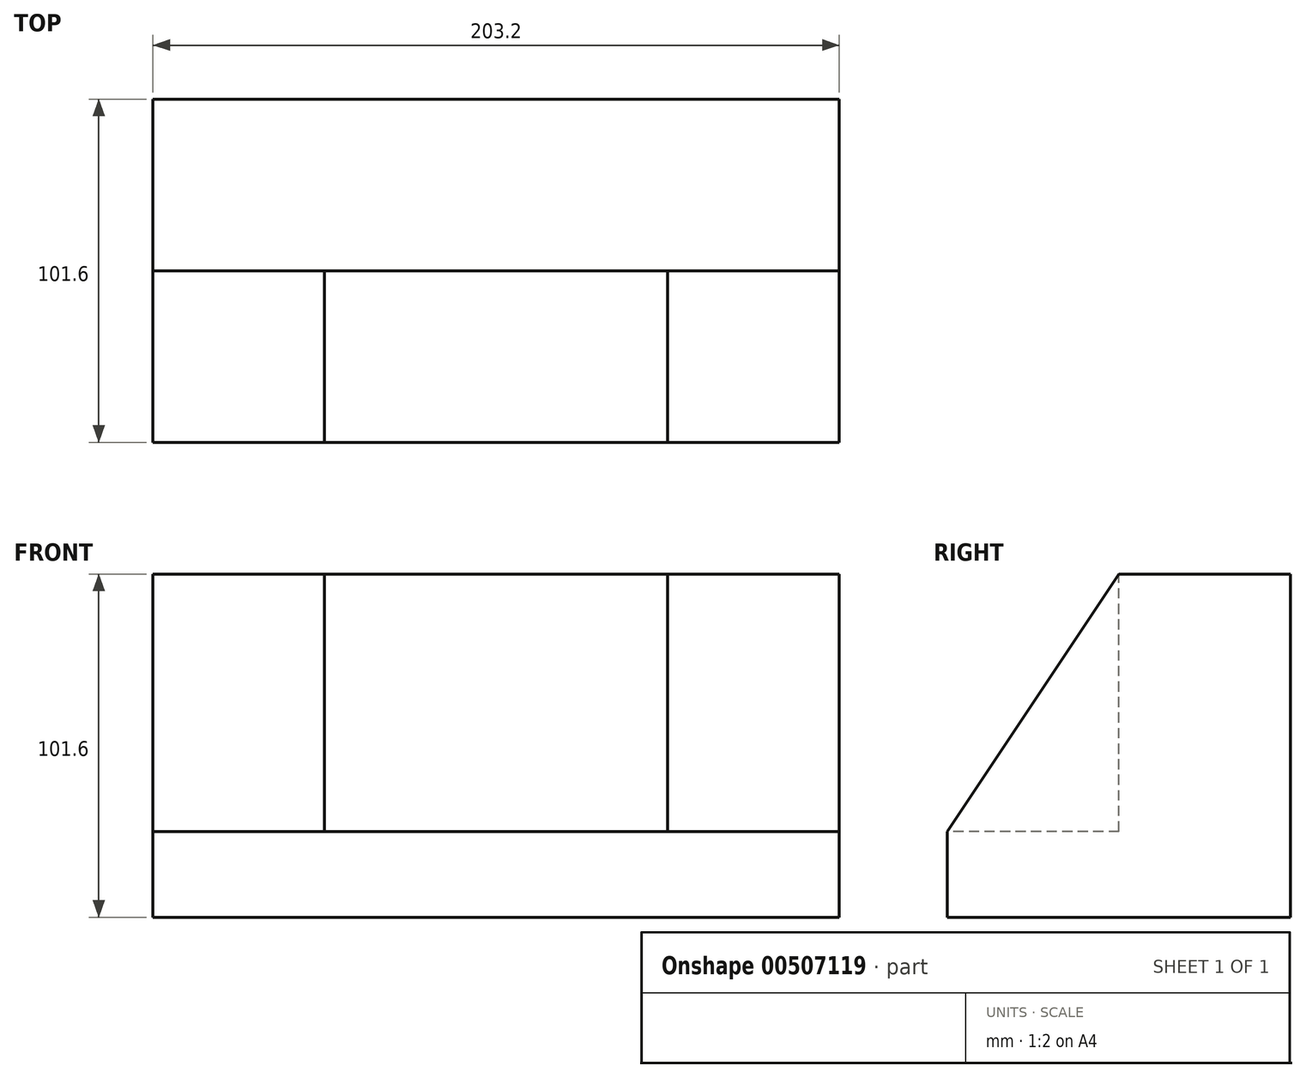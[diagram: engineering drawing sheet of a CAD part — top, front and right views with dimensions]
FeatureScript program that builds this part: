
annotation { "Feature Type Name" : "Feature", "Feature Type Description" : "" }
export const myFeature = defineFeature(function(context is Context, id is Id, definition is map)
    precondition{}
    {
        {
            var Q0;
            Q0=qCreatedBy(makeId("Top.planeOp"),FACE);
            var sketch = newSketch(context, id + "F0", { "sketchPlane" : qUnion([Q0])});
            skLineSegment(sketch, "E0.bottom", {"start": v(101.6, 50.8) * mm, "end": v(-101.6, 50.8) * mm});
            skLineSegment(sketch, "E0.top", {"start": v(101.6, -50.8) * mm, "end": v(-101.6, -50.8) * mm});
            skLineSegment(sketch, "E0.left", {"start": v(101.6, 50.8) * mm, "end": v(101.6, -50.8) * mm});
            skLineSegment(sketch, "E0.right", {"start": v(-101.6, 50.8) * mm, "end": v(-101.6, -50.8) * mm});
            skPoint(sketch, "E0.middle", {"position": v(0, 0) * mm});
            skSolve(sketch);
        }
        {
            var Q0;
            Q0=makeQuery(id+"F0.imprint","IMPRINT",FACE,{"disambiguationData":[TD([[makeQuery(id+"F0.imprint","IMPRINT",EDGE,{"derivedFrom":sQuery(id+"F0.wireOp",EDGE,"E0.bottom")}),1.0]])]});
            extrude(context, id + "F1", {"entities" : qUnion([Q0]), "depth" : 101.6 * mm});
        }
        {
            var Q0;
            Q0=makeQuery(id+"F1.opExtrude","CAP_FACE",FACE,{"disambiguationData":[OSD([sQuery(id+"F0.wireOp",EDGE,"E0.bottom"),sQuery(id+"F0.wireOp",EDGE,"E0.top"),sQuery(id+"F0.wireOp",EDGE,"E0.left"),sQuery(id+"F0.wireOp",EDGE,"E0.right")])],"isStart":false});
            var sketch = newSketch(context, id + "F2", { "sketchPlane" : qUnion([Q0])});
            skLineSegment(sketch, "E1.bottom", {"start": v(-101.6, -50.8) * mm, "end": v(101.6, -50.8) * mm});
            skLineSegment(sketch, "E1.top", {"start": v(-101.6, 0) * mm, "end": v(101.6, 0) * mm});
            skLineSegment(sketch, "E1.left", {"start": v(-101.6, -50.8) * mm, "end": v(-101.6, 0) * mm});
            skLineSegment(sketch, "E1.right", {"start": v(101.6, -50.8) * mm, "end": v(101.6, 0) * mm});
            skSolve(sketch);
        }
        {
            var Q0;
            Q0 = qSketchRegion(id + "F2", true);
            extrude(context, id + "F3", {"entities" : qUnion([Q0]), "operationType" : NewBodyOperationType.REMOVE, "oppositeDirection" : true, "depth" : 76.2 * mm});
        }
        {
            var Q0;
            Q0=makeQuery(id+"F1.opExtrude","SWEPT_FACE",FACE,{"disambiguationData":[OSD([sQuery(id+"F0.wireOp",EDGE,"E0.left")])]});
            var sketch = newSketch(context, id + "F4", { "sketchPlane" : qUnion([Q0])});
            skLineSegment(sketch, "E2", {"start": v(0, 101.6) * mm, "end": v(-50.8, 25.4) * mm});
            skLineSegment(sketch, "E3", {"start": v(-50.8, 25.4) * mm, "end": v(0, 25.4) * mm});
            skLineSegment(sketch, "E4", {"start": v(0, 25.4) * mm, "end": v(0, 101.6) * mm});
            skSolve(sketch);
        }
        {
            var Q0;
            Q0 = qSketchRegion(id + "F4", true);
            extrude(context, id + "F5", {"entities" : qUnion([Q0]), "operationType" : NewBodyOperationType.ADD, "oppositeDirection" : true, "depth" : 50.8 * mm});
        }
        {
            var Q0;
            Q0=makeQuery(id+"F1.opExtrude","SWEPT_FACE",FACE,{"disambiguationData":[OSD([sQuery(id+"F0.wireOp",EDGE,"E0.right")])]});
            var sketch = newSketch(context, id + "F6", { "sketchPlane" : qUnion([Q0])});
            skLineSegment(sketch, "E5", {"start": v(0, 101.6) * mm, "end": v(50.8, 25.4) * mm});
            skLineSegment(sketch, "E6", {"start": v(50.8, 25.4) * mm, "end": v(0, 25.4) * mm});
            skLineSegment(sketch, "E7", {"start": v(0, 25.4) * mm, "end": v(0, 101.6) * mm});
            skSolve(sketch);
        }
        {
            var Q0;
            Q0 = qSketchRegion(id + "F6", true);
            extrude(context, id + "F7", {"entities" : qUnion([Q0]), "operationType" : NewBodyOperationType.ADD, "oppositeDirection" : true, "depth" : 50.8 * mm});
        }
    });
